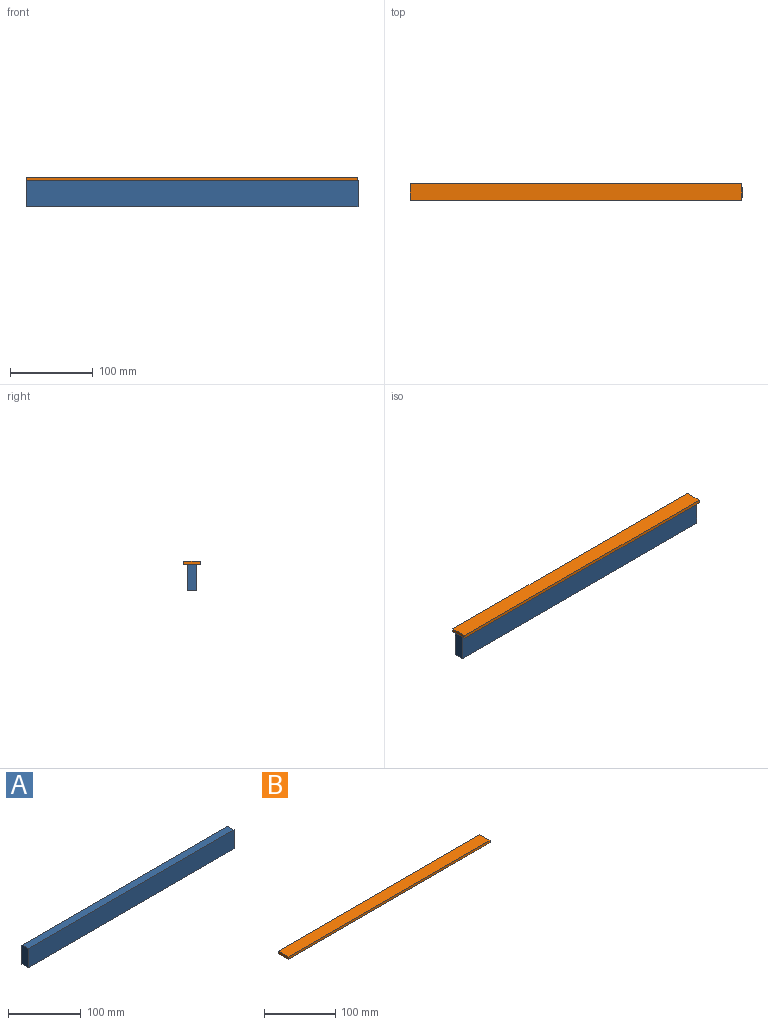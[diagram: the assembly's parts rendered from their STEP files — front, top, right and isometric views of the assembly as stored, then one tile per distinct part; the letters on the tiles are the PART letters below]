
ASSEMBLY  parts=2 mates=1
PART A: 6 faces, bbox 400x12x32 mm
  f0: plane 32x12mm, normal (1,0,0), area 384mm2, adj f1,f3,f4,f5
  f1: plane 400x12mm, normal (0,0,1), area 4800mm2, adj f0,f2,f4,f5
  f2: plane 32x12mm, normal (-1,0,0), area 384mm2, adj f1,f3,f4,f5
  f3: plane 400x12mm, normal (0,0,-1), area 4800mm2, adj f0,f2,f4,f5
  f4: plane 400x32mm, normal (0,-1,0), area 12800mm2, adj f0,f1,f2,f3
  f5: plane 400x32mm, normal (0,1,0), area 12800mm2, adj f0,f1,f2,f3
PART B: 6 faces, bbox 400x20x4 mm
  f0: plane 20x4mm, normal (1,0,0), area 80mm2, adj f1,f3,f4,f5
  f1: plane 400x20mm, normal (0,0,1), area 8000mm2, adj f0,f2,f4,f5
  f2: plane 20x4mm, normal (-1,0,0), area 80mm2, adj f1,f3,f4,f5
  f3: plane 400x20mm, normal (0,0,-1), area 8000mm2, adj f0,f2,f4,f5
  f4: plane 400x4mm, normal (0,-1,0), area 1600mm2, adj f0,f1,f2,f3
  f5: plane 400x4mm, normal (0,1,0), area 1600mm2, adj f0,f1,f2,f3
PLACE A t=(25.67,-87.51,62.41)mm
PLACE B t=(25.67,-83.51,30.71)mm
MATE fastened B.f3 <-> A.f1  axis (0,0,-1) through (-174.33,-93.51,26.71)mm
